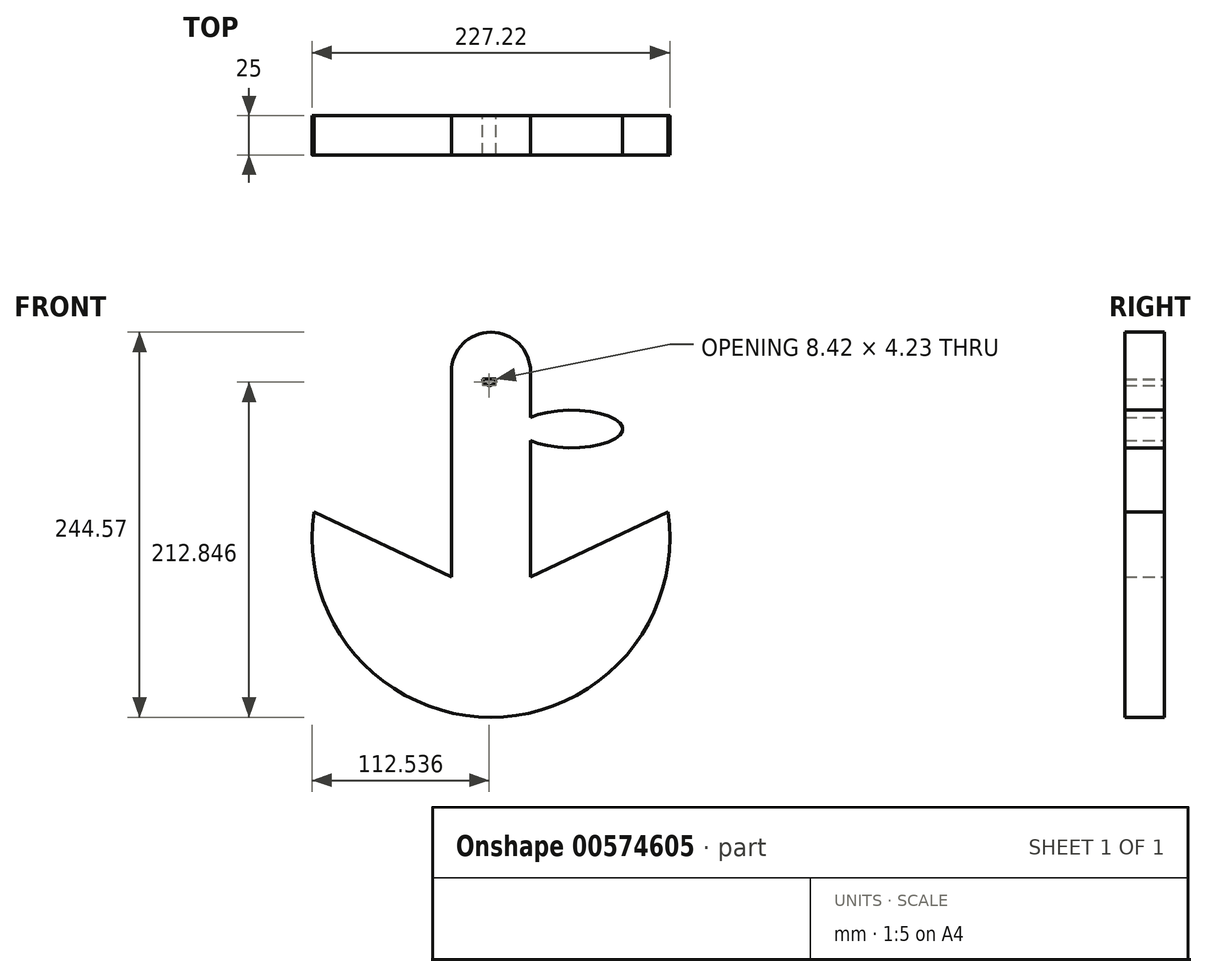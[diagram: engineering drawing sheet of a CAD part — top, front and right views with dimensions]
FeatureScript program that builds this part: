
annotation { "Feature Type Name" : "Feature", "Feature Type Description" : "" }
export const myFeature = defineFeature(function(context is Context, id is Id, definition is map)
    precondition{}
    {
        {
            var Q0;
            Q0=qCreatedBy(makeId("Front.planeOp"),FACE);
            var sketch = newSketch(context, id + "F0", { "sketchPlane" : qUnion([Q0])});
            skLineSegment(sketch, "E0", {"start": v(-25.16, 88.98) * mm, "end": v(-25.16, -94.81) * mm});
            skLineSegment(sketch, "E1", {"start": v(25.16, 88.98) * mm, "end": v(25.16, -94.81) * mm});
            skLineSegment(sketch, "E2", {"start": v(-25.16, -41.4) * mm, "end": v(-83.67, -13.62) * mm});
            skLineSegment(sketch, "E3", {"start": v(25.16, -41.4) * mm, "end": v(83.67, -13.62) * mm});
            skArc(sketch, "E4", {"start": v(-83.67, -13.62) * mm, "mid": v(0, -98.68) * mm, "end": v(83.67, -13.62) * mm});
            skArc(sketch, "E5", {"start": v(-112.35, 0) * mm, "mid": v(0, -130.43) * mm, "end": v(112.35, 0) * mm});
            skLineSegment(sketch, "E6", {"start": v(83.67, -13.62) * mm, "end": v(112.35, 0) * mm});
            skLineSegment(sketch, "E7", {"start": v(-83.67, -13.62) * mm, "end": v(-112.35, 0) * mm});
            skLineSegment(sketch, "E8", {"start": v(0, -98.68) * mm, "end": v(0, -130.43) * mm, "construction": true});
            skPoint(sketch, "E8.startSnap0", {"position": v(0, -98.68) * mm});
            skArc(sketch, "E9", {"start": v(-25.16, 88.98) * mm, "mid": v(0, 114.14) * mm, "end": v(25.16, 88.98) * mm});
            skLineSegment(sketch, "E10", {"start": v(25.16, 52.64) * mm, "end": v(83.67, 52.64) * mm});
            skEllipticalArc(sketch, "E11", {});
            skArc(sketch, "E12", {"start": v(25.16, 76.83) * mm, "mid": v(0, 84.53) * mm, "end": v(-25.16, 76.83) * mm});
            skArc(sketch, "E13", {"start": v(-25.16, 76.83) * mm, "mid": v(0, 69.66) * mm, "end": v(25.16, 76.83) * mm});
            skPoint(sketch, "E14", {"position": v(0, 114.14) * mm});
            skArc(sketch, "E15", {"start": v(-5.28, 84.22) * mm, "mid": v(-0.98, 80.3) * mm, "end": v(3.14, 84.42) * mm});
            const initialGuessF0  = {"E11": [0.05109253525733948, 0.052636537700891495, 1, 0, 0.032579792446513364, 0.011969459104448507, 3.7915729533442075, 2.491612353835307]};
            skSetInitialGuess(sketch, initialGuessF0);
            skSolve(sketch);
        }
        {
            var Q0;
            Q0 = qSketchRegion(id + "F0", true);
            extrude(context, id + "F1", {"entities" : qUnion([Q0]), "depth" : 25 * mm, "offsetDistance" : 25 * mm});
        }
    });
